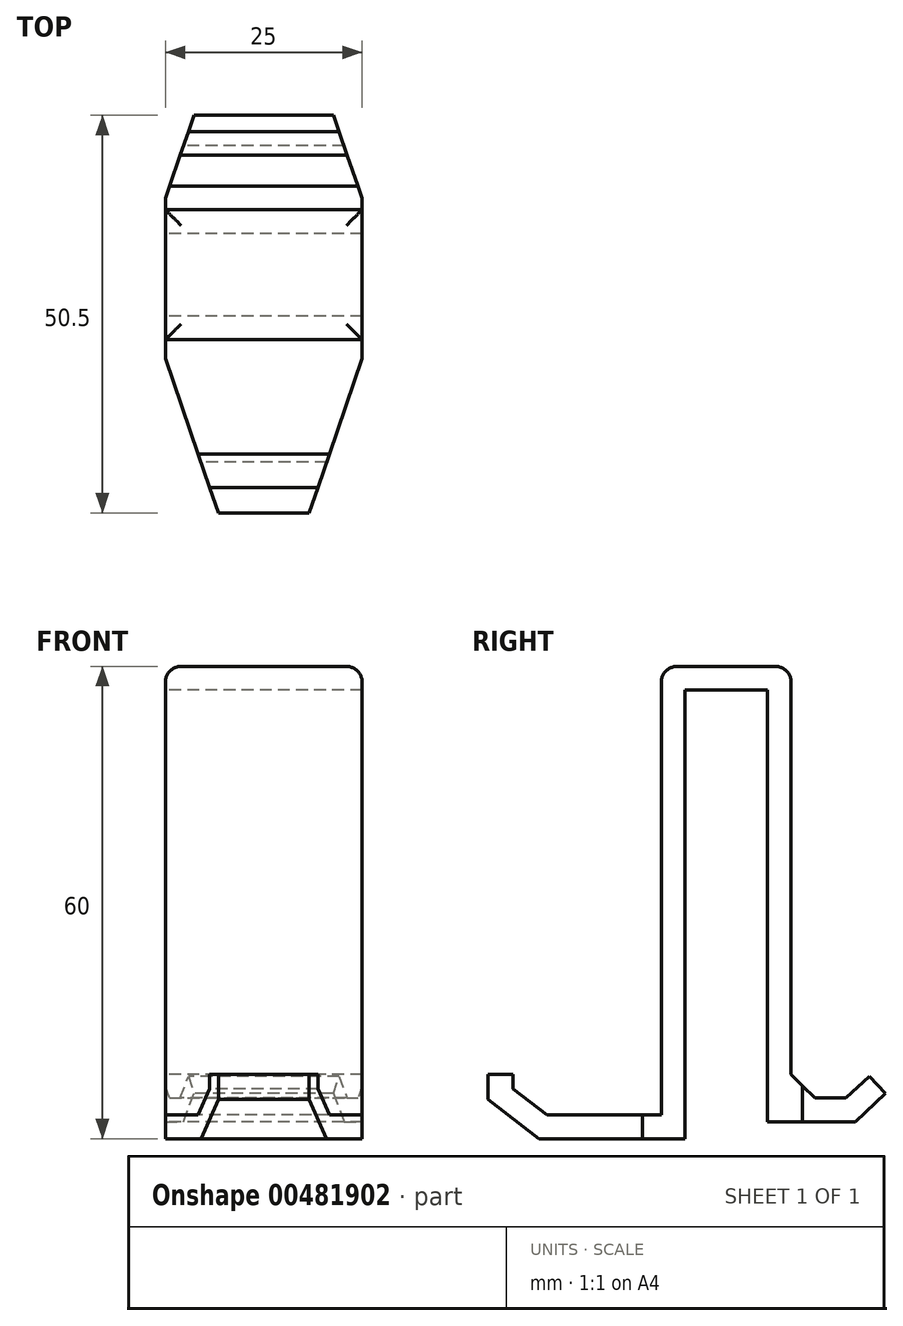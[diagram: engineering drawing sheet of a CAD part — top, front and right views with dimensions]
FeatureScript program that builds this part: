
annotation { "Feature Type Name" : "Feature", "Feature Type Description" : "" }
export const myFeature = defineFeature(function(context is Context, id is Id, definition is map)
    precondition{}
    {
        {
            var Q0;
            Q0=qCreatedBy(makeId("Right.planeOp"),FACE);
            var sketch = newSketch(context, id + "F0", { "sketchPlane" : qUnion([Q0])});
            skLineSegment(sketch, "E0", {"start": v(-4.77, 41.52) * mm, "end": v(5.73, 41.52) * mm});
            skLineSegment(sketch, "E1", {"start": v(5.73, 41.52) * mm, "end": v(5.73, -13.32) * mm});
            skLineSegment(sketch, "E2", {"start": v(5.73, -13.32) * mm, "end": v(16.87, -13.32) * mm});
            skLineSegment(sketch, "E3", {"start": v(16.87, -13.32) * mm, "end": v(20.73, -9.75) * mm});
            skLineSegment(sketch, "E4", {"start": v(-4.77, 41.52) * mm, "end": v(-4.77, -15.48) * mm});
            skLineSegment(sketch, "E5", {"start": v(-4.77, -15.48) * mm, "end": v(-23.33, -15.48) * mm});
            skLineSegment(sketch, "E6", {"start": v(-23.33, -15.48) * mm, "end": v(-29.77, -10.5) * mm});
            skLineSegment(sketch, "E7.0", {"start": v(-22.3, -12.48) * mm, "end": v(-26.58, -9.17) * mm});
            skLineSegment(sketch, "E7.1", {"start": v(-7.77, -12.48) * mm, "end": v(-22.3, -12.48) * mm});
            skLineSegment(sketch, "E7.2", {"start": v(-7.77, 44.52) * mm, "end": v(-7.77, -12.48) * mm});
            skLineSegment(sketch, "E7.3", {"start": v(15.7, -10.32) * mm, "end": v(18.69, -7.55) * mm});
            skLineSegment(sketch, "E7.4", {"start": v(8.73, -10.32) * mm, "end": v(15.7, -10.32) * mm});
            skLineSegment(sketch, "E7.5", {"start": v(8.73, 44.52) * mm, "end": v(8.73, -10.32) * mm});
            skLineSegment(sketch, "E7.6", {"start": v(-7.77, 44.52) * mm, "end": v(8.73, 44.52) * mm});
            skLineSegment(sketch, "E8", {"start": v(-29.77, -10.5) * mm, "end": v(-29.77, -7.28) * mm});
            skLineSegment(sketch, "E9", {"start": v(-26.58, -9.17) * mm, "end": v(-26.58, -7.28) * mm});
            skLineSegment(sketch, "E10", {"start": v(-26.58, -7.28) * mm, "end": v(-29.77, -7.28) * mm});
            skLineSegment(sketch, "E11", {"start": v(18.69, -7.55) * mm, "end": v(20.73, -9.75) * mm});
            skSolve(sketch);
        }
        {
            var Q0;
            Q0 = qSketchRegion(id + "F0", true);
            extrude(context, id + "F1", {"entities" : qUnion([Q0]), "depth" : 25 * mm});
        }
        {
            var Q0;
            Q0=makeQuery(id+"F1.opExtrude","SWEPT_FACE",FACE,{"disambiguationData":[OSD([sQuery(id+"F0.wireOp",EDGE,"E5")])]});
            var sketch = newSketch(context, id + "F2", { "sketchPlane" : qUnion([Q0])});
            skLineSegment(sketch, "E12", {"start": v(25, 10.18) * mm, "end": v(16.99, 33.54) * mm});
            skLineSegment(sketch, "E13", {"start": v(8.04, 33.54) * mm, "end": v(0, 10.18) * mm});
            skPoint(sketch, "E14.endSnap0", {"position": v(12.5, 23.33) * mm});
            skLineSegment(sketch, "E15", {"start": v(8.04, 33.54) * mm, "end": v(-5.28, 33.54) * mm});
            skLineSegment(sketch, "E16", {"start": v(-5.28, 33.54) * mm, "end": v(-5.28, 10.23) * mm});
            skLineSegment(sketch, "E17", {"start": v(-5.28, 10.23) * mm, "end": v(0, 10.18) * mm});
            skLineSegment(sketch, "E18", {"start": v(25, 10.18) * mm, "end": v(32.63, 10.18) * mm});
            skLineSegment(sketch, "E19", {"start": v(32.63, 10.18) * mm, "end": v(32.63, 33.54) * mm});
            skLineSegment(sketch, "E20", {"start": v(32.63, 33.54) * mm, "end": v(16.99, 33.54) * mm});
            skLineSegment(sketch, "E21.MirrorCS", {"start": v(8.04, -33.54) * mm, "end": v(-5.28, -33.54) * mm});
            skLineSegment(sketch, "E22.MirrorCS", {"start": v(25, -10.18) * mm, "end": v(16.99, -33.54) * mm});
            skLineSegment(sketch, "E23.MirrorCS", {"start": v(32.63, -10.18) * mm, "end": v(32.63, -33.54) * mm});
            skLineSegment(sketch, "E24.MirrorCS", {"start": v(-5.28, -33.54) * mm, "end": v(-5.28, -10.23) * mm});
            skLineSegment(sketch, "E25.MirrorCS", {"start": v(8.04, -33.54) * mm, "end": v(0, -10.18) * mm});
            skLineSegment(sketch, "E26.MirrorCS", {"start": v(32.63, -33.54) * mm, "end": v(16.99, -33.54) * mm});
            skPoint(sketch, "E27.MirrorP", {"position": v(12.5, -23.33) * mm});
            skLineSegment(sketch, "E28.MirrorCS", {"start": v(-5.28, -10.23) * mm, "end": v(0, -10.18) * mm});
            skLineSegment(sketch, "E29.MirrorCS", {"start": v(25, -10.18) * mm, "end": v(32.63, -10.18) * mm});
            skSolve(sketch);
        }
        {
            var Q0;
            Q0 = qSketchRegion(id + "F2", true);
            extrude(context, id + "F3", {"entities" : qUnion([Q0]), "operationType" : NewBodyOperationType.REMOVE, "oppositeDirection" : true, "depth" : 25 * mm});
        }
        {
            var Q0;
            Q0=makeQuery(id+"F1.opExtrude","SWEPT_EDGE",EDGE,{"disambiguationData":[OSD([sQuery(id+"F0.wireOp",EDGE,"E7.2"),sQuery(id+"F0.wireOp",EDGE,"E7.6")])]});
            var Q1;
            Q1=makeQuery(id+"F1.opExtrude","CAP_EDGE",EDGE,{"disambiguationData":[OSD([sQuery(id+"F0.wireOp",EDGE,"E7.6")])],"isStart":false});
            var Q2;
            Q2=makeQuery(id+"F1.opExtrude","SWEPT_EDGE",EDGE,{"disambiguationData":[OSD([sQuery(id+"F0.wireOp",EDGE,"E7.5"),sQuery(id+"F0.wireOp",EDGE,"E7.6")])]});
            var Q3;
            Q3=makeQuery(id+"F1.opExtrude","CAP_EDGE",EDGE,{"disambiguationData":[OSD([sQuery(id+"F0.wireOp",EDGE,"E7.6")])],"isStart":true});
            fillet(context, id + "F4", {"entities" : qUnion([Q0, Q1, Q2, Q3]), "radius" : 2 * mm, "tangentPropagation" : true, "allowEdgeOverflow" : false});
        }
        {
            var Q0;
            Q0=makeQuery(id+"F1.opExtrude","SWEPT_EDGE",EDGE,{"disambiguationData":[OSD([sQuery(id+"F0.wireOp",EDGE,"E7.4"),sQuery(id+"F0.wireOp",EDGE,"E7.5")])]});
            chamfer(context, id + "F5", {"entities" : qUnion([Q0]), "width" : 3 * mm, "tangentPropagation" : true});
        }
    });
